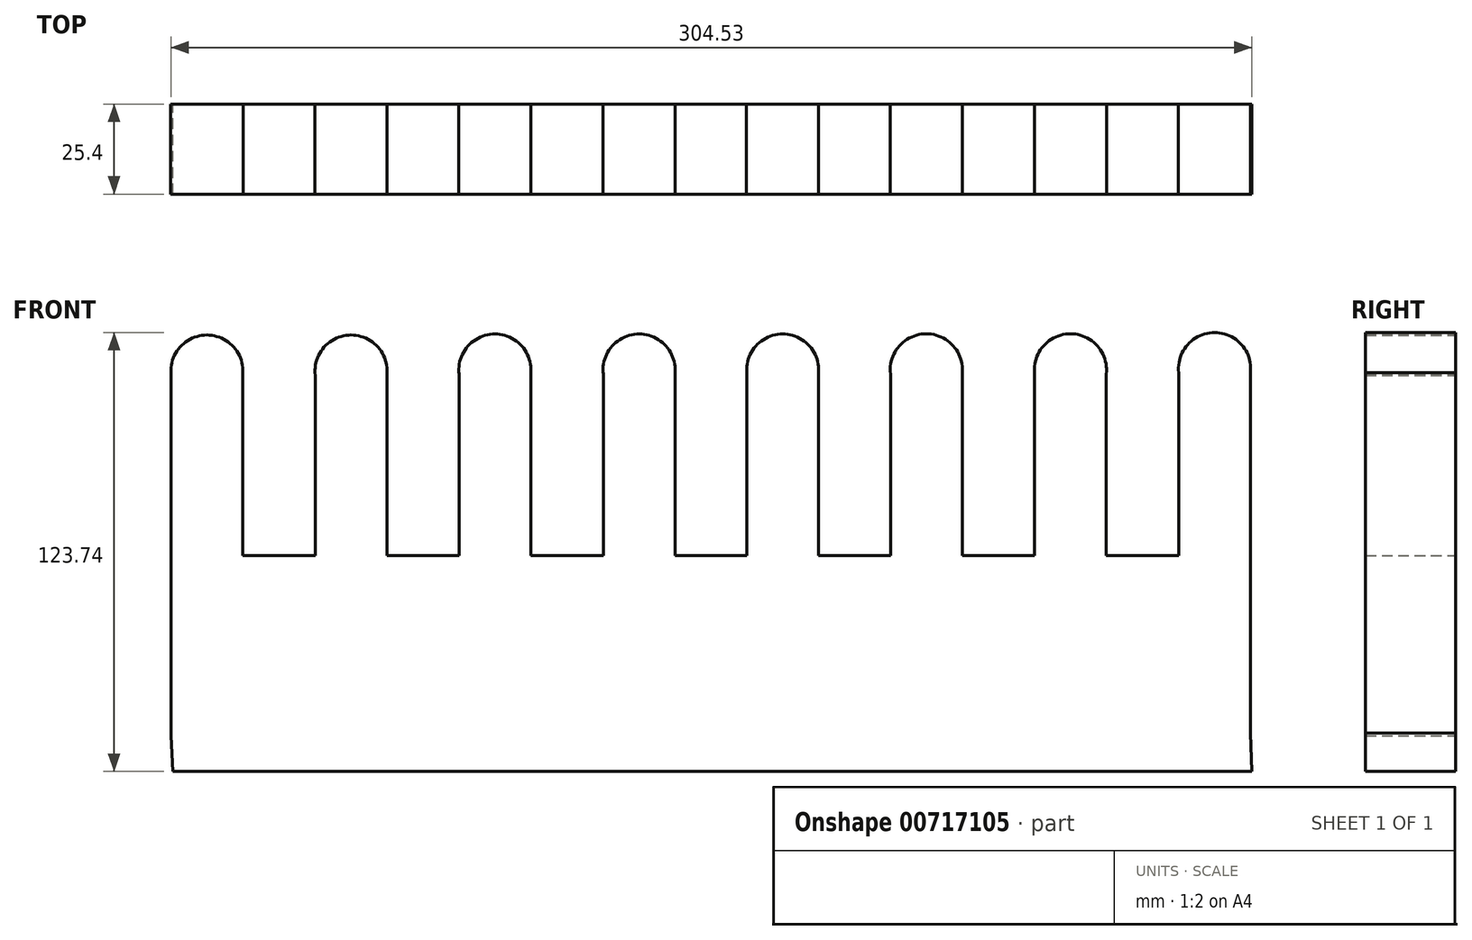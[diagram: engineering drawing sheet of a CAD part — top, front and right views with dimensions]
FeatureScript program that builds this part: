
annotation { "Feature Type Name" : "Feature", "Feature Type Description" : "" }
export const myFeature = defineFeature(function(context is Context, id is Id, definition is map)
    precondition{}
    {
        {
            var Q0;
            Q0=qCreatedBy(makeId("Front.planeOp"),FACE);
            var sketch = newSketch(context, id + "F0", { "sketchPlane" : qUnion([Q0])});
            skCircle(sketch, "E0", {"center": v(-82.84, 64.54) * mm, "radius": 10.16 * mm});
            skLineSegment(sketch, "E1", {"start": v(-72.75, 63.38) * mm, "end": v(-72.75, -38.22) * mm});
            skLineSegment(sketch, "E2", {"start": v(-92.94, 63.38) * mm, "end": v(-92.94, -38.22) * mm});
            skPoint(sketch, "E3.second.point", {"position": v(-52.43, -38.22) * mm});
            skPoint(sketch, "E3.third.point", {"position": v(-55.43, -45.42) * mm});
            skLineSegment(sketch, "E4", {"start": v(-52.31, 63.37) * mm, "end": v(-52.31, -38.23) * mm});
            skCircle(sketch, "E5", {"center": v(-42.22, 64.53) * mm, "radius": 10.16 * mm});
            skLineSegment(sketch, "E6", {"start": v(-32.13, 63.37) * mm, "end": v(-32.13, -38.23) * mm});
            skPoint(sketch, "E7.second.point", {"position": v(-11.8, -38.23) * mm});
            skPoint(sketch, "E7.third.point", {"position": v(-14.8, -45.43) * mm});
            skLineSegment(sketch, "E8", {"start": v(-11.88, 63.37) * mm, "end": v(-11.88, -38.23) * mm});
            skCircle(sketch, "E9", {"center": v(-1.78, 64.53) * mm, "radius": 10.16 * mm});
            skLineSegment(sketch, "E10", {"start": v(8.31, 63.37) * mm, "end": v(8.31, -38.23) * mm});
            skPoint(sketch, "E11.second.point", {"position": v(28.63, -38.23) * mm});
            skPoint(sketch, "E11.third.point", {"position": v(25.64, -45.43) * mm});
            skLineSegment(sketch, "E12", {"start": v(28.59, 63.45) * mm, "end": v(28.59, -38.15) * mm});
            skCircle(sketch, "E13", {"center": v(38.68, 64.6) * mm, "radius": 10.16 * mm});
            skLineSegment(sketch, "E14", {"start": v(48.78, 63.45) * mm, "end": v(48.78, -38.15) * mm});
            skPoint(sketch, "E15.second.point", {"position": v(69.1, -38.15) * mm});
            skPoint(sketch, "E15.third.point", {"position": v(66.1, -45.36) * mm});
            skLineSegment(sketch, "E16", {"start": v(69.18, 63.45) * mm, "end": v(69.18, -38.15) * mm});
            skCircle(sketch, "E17", {"center": v(79.28, 64.6) * mm, "radius": 10.16 * mm});
            skLineSegment(sketch, "E18", {"start": v(89.37, 63.45) * mm, "end": v(89.37, -38.15) * mm});
            skPoint(sketch, "E19.second.point", {"position": v(109.7, -38.15) * mm});
            skPoint(sketch, "E19.third.point", {"position": v(106.7, -45.36) * mm});
            skLineSegment(sketch, "E20", {"start": v(109.78, 63.8) * mm, "end": v(109.78, -37.8) * mm});
            skCircle(sketch, "E21", {"center": v(119.88, 64.96) * mm, "radius": 10.16 * mm});
            skLineSegment(sketch, "E22", {"start": v(129.97, 63.8) * mm, "end": v(129.97, -37.8) * mm});
            skLineSegment(sketch, "E23", {"start": v(-133.45, 63.1) * mm, "end": v(-133.45, -38.5) * mm});
            skCircle(sketch, "E24", {"center": v(-123.36, 64.25) * mm, "radius": 10.16 * mm});
            skLineSegment(sketch, "E25", {"start": v(-113.26, 63.1) * mm, "end": v(-113.26, -38.5) * mm});
            skPoint(sketch, "E26.second.point", {"position": v(-92.94, -38.5) * mm});
            skPoint(sketch, "E26.third.point", {"position": v(-95.94, -45.71) * mm});
            skLineSegment(sketch, "E27", {"start": v(-174.05, 63.1) * mm, "end": v(-174.05, -38.5) * mm});
            skCircle(sketch, "E28", {"center": v(-163.95, 64.25) * mm, "radius": 10.16 * mm});
            skLineSegment(sketch, "E29", {"start": v(-153.86, 63.1) * mm, "end": v(-153.86, -38.5) * mm});
            skPoint(sketch, "E30.second.point", {"position": v(-133.54, -38.5) * mm});
            skPoint(sketch, "E30.third.point", {"position": v(-136.54, -45.71) * mm});
            skLineSegment(sketch, "E31", {"start": v(-144.62, -48.62) * mm, "end": v(130.42, -48.62) * mm});
            skLineSegment(sketch, "E32", {"start": v(-144.62, -48.62) * mm, "end": v(-173.53, -48.62) * mm});
            skLineSegment(sketch, "E33", {"start": v(129.97, -37.8) * mm, "end": v(130.42, -48.62) * mm});
            skLineSegment(sketch, "E34", {"start": v(-174.05, -38.5) * mm, "end": v(-173.53, -48.62) * mm});
            skLineSegment(sketch, "E35", {"start": v(-174.05, 12.3) * mm, "end": v(129.97, 12.3) * mm});
            skSolve(sketch);
        }
        {
            var Q0;
            Q0=qSketchRegion(id+"F0",true);
            extrude(context, id + "F1", {"entities" : qUnion([Q0]), "depth" : 25.4 * mm});
        }
    });
